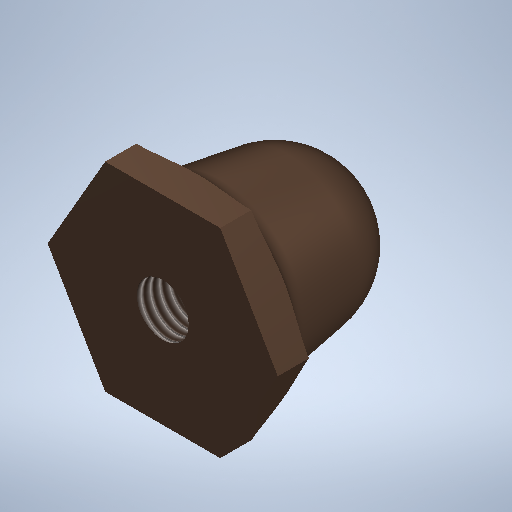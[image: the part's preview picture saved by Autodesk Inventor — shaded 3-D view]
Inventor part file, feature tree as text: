
AUTODESK INVENTOR PART (.ipt)
format: ipt  version: 2025 (Build 290162010, 162A)  size: 303,616 bytes
history: native  units: mm
features: sketch x4, extrude x2, projected_geometry x2, revolve x1, hole x1
ambient origin geometry x8: Origin, YZ Plane, XZ Plane, XY Plane, X Axis, Y Axis, Z Axis, Center Point
bodies: Volumenkörper1 (feature_tree)
feature tree (10):
  extrude  "Extrusion1"  Depth=5.0mm TaperAngle=0.0deg
  revolve  "Umdrehung1"
  extrude  "Extrusion4"  Depth=5.0mm
  hole  "Bohrung1"  [1 undecoded]
  sketch  "Skizze2"  dims[d8=37.0mm d9=5.0mm d10=0.0mm]
  sketch  "Skizze4"  dims[d11=12.0mm d12=5.0mm]
  sketch  "Skizze5"  dims[d13=30.0mm d15=90.0deg]
  projected_geometry  "Projizierte Kontur1"
  projected_geometry  "Projizierte Kontur2"
  sketch  "Skizze6"  dims[d20=5.0mm d21=0.0mm d22=8.376mm d23=23.0mm d24=4.0mm d25=2.0mm d26=90.0deg d27=25.0mm d28=20.594885mm]
note: 1 required parameter value undecoded (feature->parameter linkage not recoverable at this tier; creation-order binding heuristic only, values carry confidence <= 0.55)
